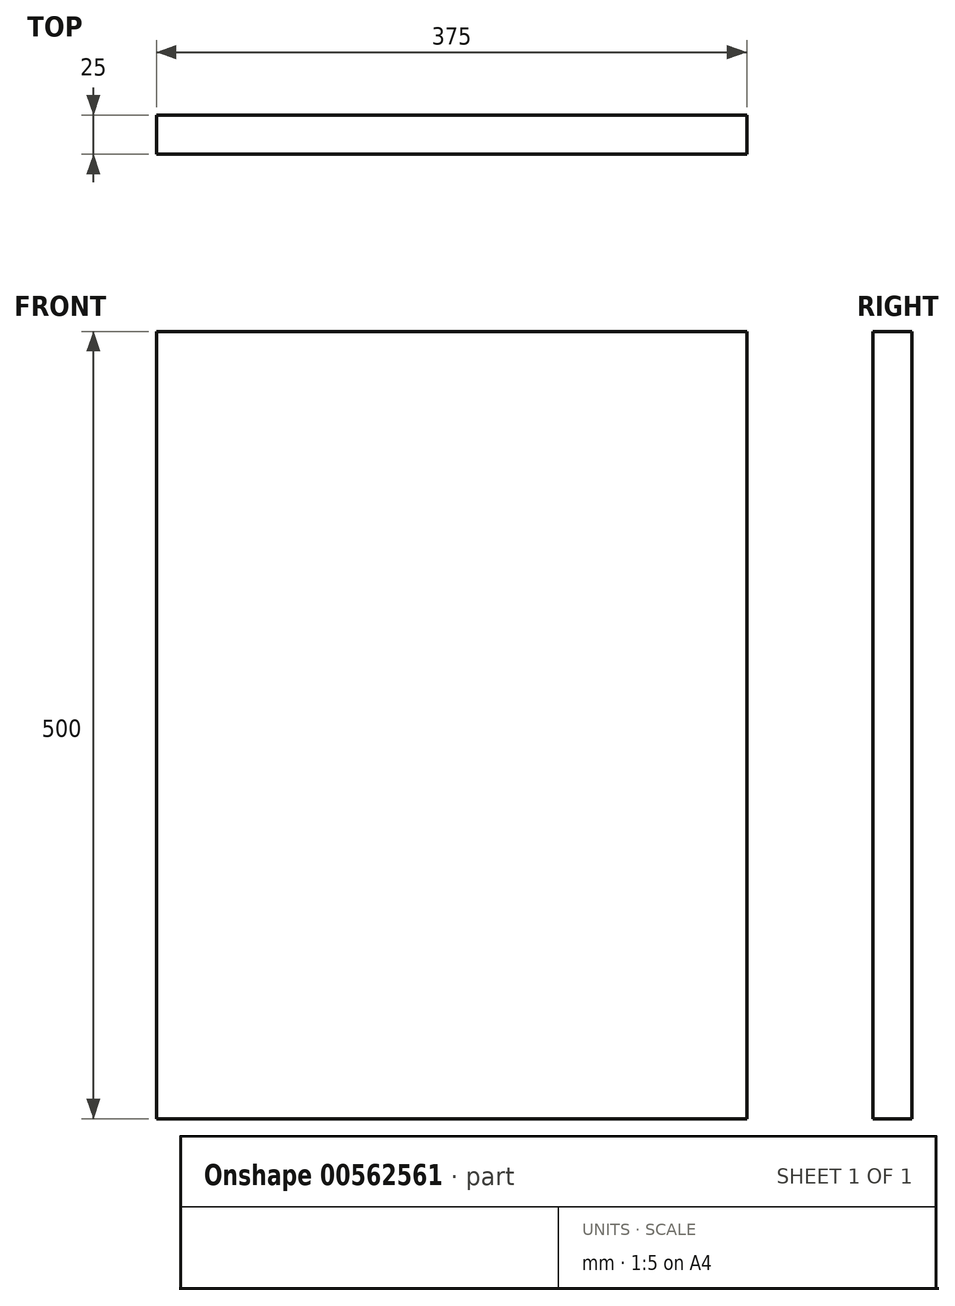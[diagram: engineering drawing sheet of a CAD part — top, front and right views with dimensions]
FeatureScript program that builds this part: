
annotation { "Feature Type Name" : "Feature", "Feature Type Description" : "" }
export const myFeature = defineFeature(function(context is Context, id is Id, definition is map)
    precondition{}
    {
        {
            var Q0;
            Q0=qCreatedBy(makeId("Front.planeOp"),FACE);
            var sketch = newSketch(context, id + "F0", { "sketchPlane" : qUnion([Q0])});
            skLineSegment(sketch, "E0.bottom", {"start": v(0, 0) * mm, "end": v(375, 0) * mm});
            skLineSegment(sketch, "E0.top", {"start": v(0, 500) * mm, "end": v(375, 500) * mm});
            skLineSegment(sketch, "E0.left", {"start": v(0, 0) * mm, "end": v(0, 500) * mm});
            skLineSegment(sketch, "E0.right", {"start": v(375, 0) * mm, "end": v(375, 500) * mm});
            skSolve(sketch);
        }
        {
            var Q0;
            Q0 = qSketchRegion(id + "F0", true);
            var Q1;
            Q1=makeQuery(id+"F0.imprint","IMPRINT",FACE,{"disambiguationData":[TD([[makeQuery(id+"F0.imprint","IMPRINT",EDGE,{"derivedFrom":sQuery(id+"F0.wireOp",EDGE,"E0.bottom")}),1.0]])]});
            extrude(context, id + "F1", {"entities" : qUnion([Q0, Q1]), "depth" : 25 * mm, "offsetDistance" : 25 * mm});
        }
    });
